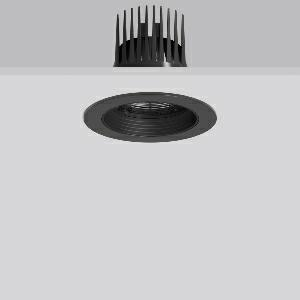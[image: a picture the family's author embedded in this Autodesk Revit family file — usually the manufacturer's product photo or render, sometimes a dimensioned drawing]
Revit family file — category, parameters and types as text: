
# Revit family: heledon_maxi_e_901769_003_1_caa3
name_source: partatom
category: Lighting Fixtures
units: mm (PartAtom-declared; Revit-internal decimal feet)

## family parameters
Cut with Voids When Loaded = No
Host = Face
Light Source = No
Part Type = Normal
Room Calculation Point = No
Round Connector Dimension = Use Diameter
Shared = No

## types (1)
- HELEDON maxi E (1 x LED Modul 940, 3800 lm, 4000)
    Apparent Load = 35 VA
    Approval mark = CE
    CIE Flux Codes = 96 100 100 100 100
    Color Rendering = 92
    Color Temperature = 4000
    Default Elevation = 1800 mm
    Description = Series: HELEDON maxi
Round recessed downlight. Housing: die-cast aluminium, powder-coated. Black plastic ring and recessed LED to prevent glare from the side. Optical assembly with lens made of plastic (polycarbonate) for the best homogeneous light distribution - can be changed without tools. Best colour rendering index Ra>90. Suitable for Recessed ceiling mounting. Installation without tools thanks to spring fastening system. Including separate LED converter with connecting cable 600 mm.High quality converter without flickering and stroboscopic effect. Through-wiring box (5 pole) available as accessory. The following accessories can be mounted without use of tools: interchangeable lenses, decorative glasses, honeycomb louvre, clear and frosted diffusers, white interchangeable plastic ring. 
Colour: deep black, matt (RAL 9005)
Diameter: 162 mm
Height: 3 mm
Cut-out diameter: 152 mm
Recess height: 200 mm
Luminaire: recess height: 135 mm
Lamp: LED
Socket: without socket
Colour temperature: 4000K
Colour rendering index (CRI): 92
System power: 35 W
Rated luminous flux: 3800 lm
Luminous efficiency: 109 lm/W
Control gear: Regulated power supply
Protection class: II
Type of protection: IP 20
    Height = 0 mm  [stored 0 ft]
    Lamp = 1 x LED Modul 940
    Lamp Light Flux = 3800 lm
    Lamp count = 1
    Length = 162 mm
    Lifetime = 50000 h
    Luminous efficacy = 109 lm/W
    Manufacturer = RZB
    ModVariant = No
    Model = 901769.003.1
    Mounting Place = Ceiling
    Mounting Type = Recessed
    Number of Poles = 1
    OnlyDefault = Yes
    Power Factor = 1
    Product Name = HELEDON maxi E
    Product group = Recessed downlights
    ProductGroupID = 402
    Protection Class = Protection class II
    Protection Degree = IP 20
    RLX_Detail_Level = 1
    RLX_Emergency_Light_Flux = 0 lm
    RLX_Emergency_Type = 0
    RLX_Emergency_Type_DB = No
    RlxData = <blob elided: 121093 chars, md5=583f3add>
    Socket = socket
    Standby Power = 0 W
    System Light Flux = 3800 lm
    System Power = 35 W
    Type Comments = Product without accessories
    Type Image = 901663.003.jpg
    URL = http://relux.com
    VarID = ---
    Voltage = 230 V
    Voltage Range = 220-240 V
    Weight = 0.00 kg
    Width = 0 mm  [stored 0 ft]

note: [stored X ft] marks values corroborated as IEEE doubles in the binary element streams (Revit-internal decimal feet)

## geometry (parser evidence)
native form markers: Blend x4, Sweep x10
no freeform markers — native parametric forms only
